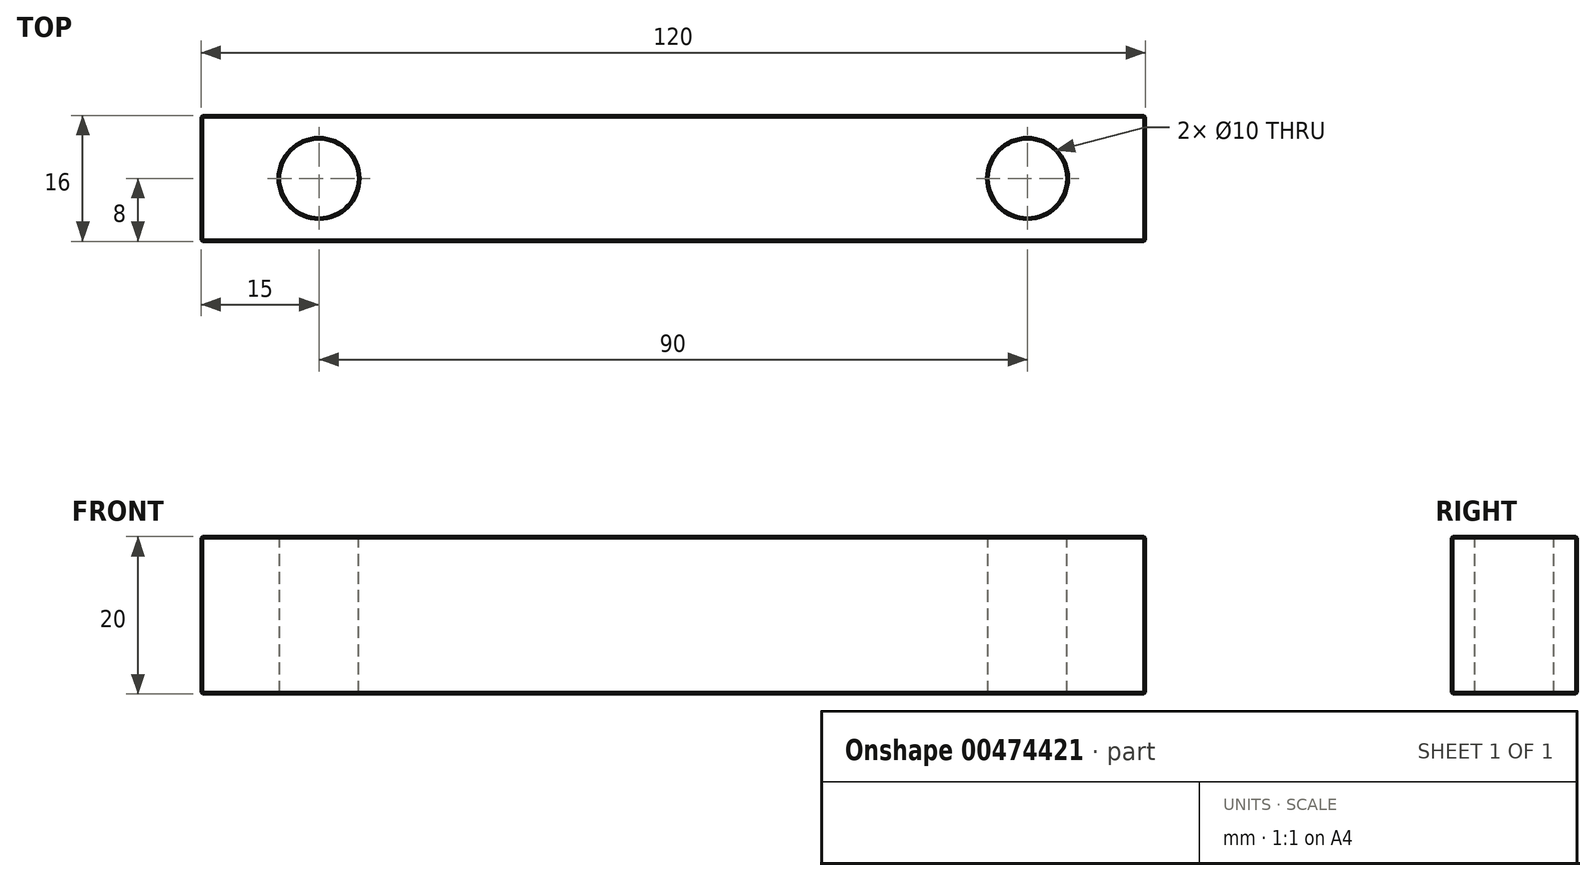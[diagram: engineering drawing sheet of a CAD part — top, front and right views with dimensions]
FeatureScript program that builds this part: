
annotation { "Feature Type Name" : "Feature", "Feature Type Description" : "" }
export const myFeature = defineFeature(function(context is Context, id is Id, definition is map)
    precondition{}
    {
        {
            var Q0;
            Q0=qCreatedBy(makeId("Top.planeOp"),FACE);
            var sketch = newSketch(context, id + "F0", { "sketchPlane" : qUnion([Q0])});
            skLineSegment(sketch, "E0.bottom", {"start": v(-60, 8) * mm, "end": v(60, 8) * mm});
            skLineSegment(sketch, "E0.top", {"start": v(-60, -8) * mm, "end": v(60, -8) * mm});
            skLineSegment(sketch, "E0.left", {"start": v(-60, 8) * mm, "end": v(-60, -8) * mm});
            skLineSegment(sketch, "E0.right", {"start": v(60, 8) * mm, "end": v(60, -8) * mm});
            skSolve(sketch);
        }
        {
            var Q0;
            Q0 = qSketchRegion(id + "F0", true);
            extrude(context, id + "F1", {"entities" : qUnion([Q0]), "oppositeDirection" : true, "depth" : 20 * mm, "offsetDistance" : 25 * mm});
        }
        {
            var Q0;
            Q0=qCreatedBy(makeId("Top.planeOp"),FACE);
            var sketch = newSketch(context, id + "F2", { "sketchPlane" : qUnion([Q0])});
            skPoint(sketch, "E1", {"position": v(45, 0) * mm});
            skPoint(sketch, "E2", {"position": v(-45, 0) * mm});
            skPoint(sketch, "E3", {"position": v(0, 0) * mm});
            skSolve(sketch);
        }
        {
            var Q0;
            Q0=sQuery(id+"F2.wireOp",VERTEX,"E2");
            var Q1;
            Q1=sQuery(id+"F2.wireOp",VERTEX,"E1");
            var Q2;
            Q2=makeQuery(id+"F1.opExtrude","SWEPT_BODY",BODY,{"disambiguationData":[OSD([sQuery(id+"F0.wireOp",EDGE,"E0.bottom"),sQuery(id+"F0.wireOp",EDGE,"E0.top"),sQuery(id+"F0.wireOp",EDGE,"E0.left"),sQuery(id+"F0.wireOp",EDGE,"E0.right")])]});
            hole(context, id + "F3", {"style" : HoleStyle.SIMPLE, "endStyle" : HoleEndStyle.THROUGH, "standardTappedOrClearance" : lookupTablePath({ "standard" : "ISO", "size" : "10", "type" : "Drilled" }), "standardBlindInLast" : lookupTablePath({ "standard" : "ISO", "size" : "10", "type" : "Drilled" }), "holeDiameter" : 10 * mm, "majorDiameter" : 5 * mm, "isTappedThrough" : true, "tappedDepth" : 12 * mm, "tapClearance" : 3, "startFromSketch" : true, "locations" : qUnion([Q0, Q1]), "scope" : qUnion([Q2])});
        }
        {
            var Q0;
            Q0=makeQuery(id+"F1.opExtrude","CAP_FACE",FACE,{"disambiguationData":[OSD([sQuery(id+"F0.wireOp",EDGE,"E0.bottom"),sQuery(id+"F0.wireOp",EDGE,"E0.top"),sQuery(id+"F0.wireOp",EDGE,"E0.left"),sQuery(id+"F0.wireOp",EDGE,"E0.right")])],"isStart":true});
            var Q1;
            Q1=makeQuery(id+"F1.opExtrude","SWEPT_FACE",FACE,{"disambiguationData":[OSD([sQuery(id+"F0.wireOp",EDGE,"E0.left")])]});
            var Q2;
            Q2=makeQuery(id+"F1.opExtrude","CAP_FACE",FACE,{"disambiguationData":[OSD([sQuery(id+"F0.wireOp",EDGE,"E0.bottom"),sQuery(id+"F0.wireOp",EDGE,"E0.top"),sQuery(id+"F0.wireOp",EDGE,"E0.left"),sQuery(id+"F0.wireOp",EDGE,"E0.right")])],"isStart":false});
            var Q3;
            Q3=makeQuery(id+"F1.opExtrude","SWEPT_FACE",FACE,{"disambiguationData":[OSD([sQuery(id+"F0.wireOp",EDGE,"E0.bottom")])]});
            var Q4;
            Q4=makeQuery(id+"F1.opExtrude","SWEPT_FACE",FACE,{"disambiguationData":[OSD([sQuery(id+"F0.wireOp",EDGE,"E0.right")])]});
            chamfer(context, id + "F4", {"entities" : qUnion([Q0, Q1, Q2, Q3, Q4]), "width" : 0.2 * mm, "tangentPropagation" : true});
        }
    });
